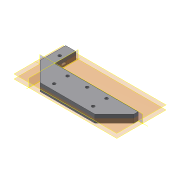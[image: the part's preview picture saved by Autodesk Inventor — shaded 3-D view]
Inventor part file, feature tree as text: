
AUTODESK INVENTOR PART (.ipt)
format: ipt  version: 2015 SP2 (Build 190223200, 223)  size: 186,368 bytes
history: native  units: mm
features: extrude x5, sketch x5, other x1, plane x1, pattern_linear x1
ambient origin geometry x8: Origin, YZ Plane, XZ Plane, XY Plane, X Axis, Y Axis, Z Axis, Center Point
bodies: Body1 (feature_tree)
feature tree (13):
  other  "Sólido1"
  extrude  "Extrusión1"  Depth=107.0mm
  extrude  "Extrusión2"  Depth=70.0mm
  extrude  "Extrusión3"  Depth=32.5mm
  plane  "Plano de trabajo1"
  extrude  "Extrusión4"  Depth=27.0mm
  pattern_linear  "Patrón rectangular1"  Spacing1=3.78mm  [1 undecoded]
  extrude  "Extrusión5"  Depth=0.8mm
  sketch  "Boceto1"  dims[d0=107.0mm d1=5.5mm]
  sketch  "Boceto2"  dims[d2=35.355mm d3=70.0mm]
  sketch  "Boceto3"  dims[d4=35.355mm d5=32.5mm]
  sketch  "Boceto4"  dims[d6=13.0mm d7=27.0mm]
  sketch  "Boceto5"  dims[d8=10.0mm d9=0.0mm d10=3.78mm d11=3.78mm d12=3.78mm d13=3.78mm d14=3.78mm d15=3.78mm d16=25.0mm d17=25.0mm d18=17.25mm d19=7.75mm d20=35.0mm d21=15.0mm d22=5.5mm d23=10.0mm d24=0.0mm d25=7.2mm d26=7.2mm d27=2.79mm d28=0.0mm d29=-4.39mm d30=7.3mm d31=6.235mm d32=3.6mm d33=6.235mm d34=3.6mm d35=7.3mm d36=3.0mm d37=0.0mm d38=30.0mm d40=-25.0mm d41=4.0mm d42=9.0mm d43=9.0mm d44=0.8mm d45=0.0mm]
note: 1 required parameter value undecoded (feature->parameter linkage not recoverable at this tier; creation-order binding heuristic only, values carry confidence <= 0.55)
